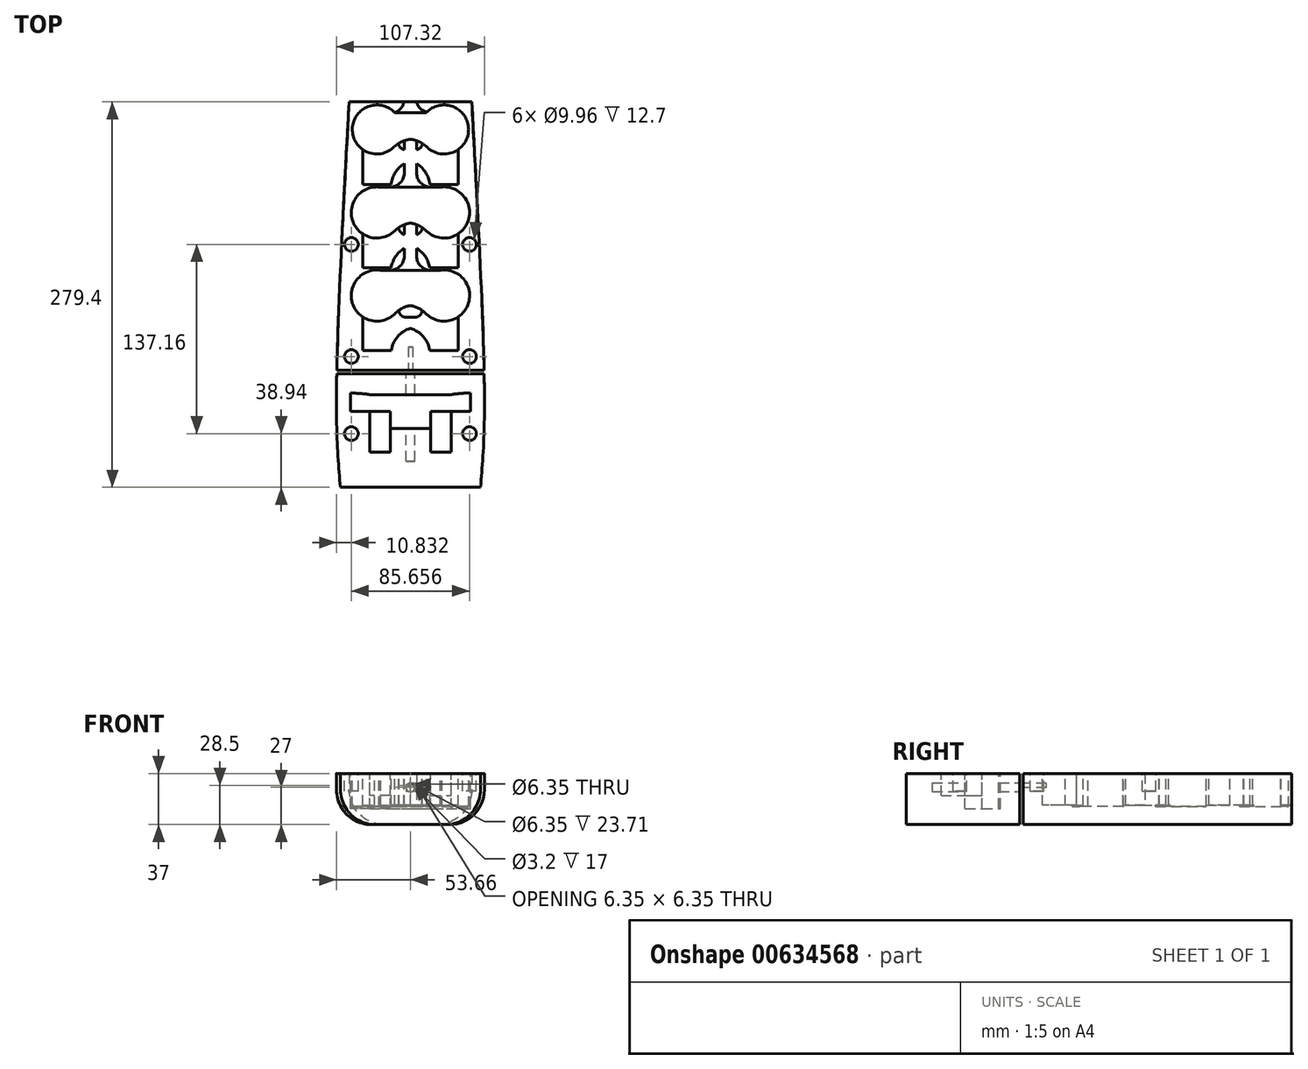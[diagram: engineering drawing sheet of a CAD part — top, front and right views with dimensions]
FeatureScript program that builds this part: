
annotation { "Feature Type Name" : "Feature", "Feature Type Description" : "" }
export const myFeature = defineFeature(function(context is Context, id is Id, definition is map)
    precondition{}
    {
        {
            var Q0;
            Q0=qCreatedBy(makeId("Top.planeOp"),FACE);
            var sketch = newSketch(context, id + "F0", { "sketchPlane" : qUnion([Q0])});
            skLineSegment(sketch, "E0", {"start": v(-44.45, 139.7) * mm, "end": v(44.45, 139.7) * mm});
            skLineSegment(sketch, "E1", {"start": v(0, 139.7) * mm, "end": v(0, -139.7) * mm, "construction": true});
            skLineSegment(sketch, "E2", {"start": v(0, -139.7) * mm, "end": v(-50.8, -139.7) * mm});
            skFitSpline(sketch, "E3", {"points": [v(-44.45, 139.7) * mm, v(-53.65, -82.07) * mm, v(-50.8, -139.7) * mm], "startDerivative": vector(-21.3, -389.22) * mm, "endDerivative": vector(12.22, -142.93) * mm});
            skFitSpline(sketch, "E4.MirrorCS", {"points": [v(44.45, 139.7) * mm, v(53.65, -82.07) * mm, v(50.8, -139.7) * mm], "startDerivative": vector(21.3, -389.22) * mm, "endDerivative": vector(-12.22, -142.93) * mm});
            skLineSegment(sketch, "E5.MirrorCS", {"start": v(0, -139.7) * mm, "end": v(50.8, -139.7) * mm});
            skSolve(sketch);
        }
        {
            var Q0;
            Q0=qSketchRegion(id+"F0",true);
            extrude(context, id + "F1", {"entities" : qUnion([Q0]), "depth" : 37 * mm, "offsetDistance" : 25.4 * mm});
        }
        {
            var Q0;
            Q0=makeQuery(id+"F1.opExtrude","CAP_EDGE",EDGE,{"disambiguationData":[OSD([sQuery(id+"F0.wireOp",EDGE,"E3")])],"isStart":true});
            var Q1;
            Q1=makeQuery(id+"F1.opExtrude","CAP_EDGE",EDGE,{"disambiguationData":[OSD([sQuery(id+"F0.wireOp",EDGE,"E4.MirrorCS")])],"isStart":true});
            fillet(context, id + "F2", {"entities" : qUnion([Q0, Q1]), "radius" : 25.4 * mm, "tangentPropagation" : true, "allowEdgeOverflow" : false});
        }
        {
            var Q0;
            Q0=makeQuery(id+"F1.opExtrude","CAP_FACE",FACE,{"disambiguationData":[OSD([sQuery(id+"F0.wireOp",EDGE,"E0"),sQuery(id+"F0.wireOp",EDGE,"E2"),sQuery(id+"F0.wireOp",EDGE,"E3"),sQuery(id+"F0.wireOp",EDGE,"E4.MirrorCS"),sQuery(id+"F0.wireOp",EDGE,"E5.MirrorCS")])],"isStart":false});
            var sketch = newSketch(context, id + "F3", { "sketchPlane" : qUnion([Q0])});
            skLineSegment(sketch, "E6.bottom", {"start": v(-34.7, 119.7) * mm, "end": v(-14, 119.7) * mm});
            skLineSegment(sketch, "E6.top", {"start": v(-34.7, 79.7) * mm, "end": v(-14, 79.7) * mm});
            skLineSegment(sketch, "E6.left", {"start": v(-34.7, 119.7) * mm, "end": v(-34.7, 79.7) * mm});
            skLineSegment(sketch, "E6.right", {"start": v(-14, 119.7) * mm, "end": v(-14, 79.7) * mm});
            skLineSegment(sketch, "E7", {"start": v(0, 139.7) * mm, "end": v(0, 0) * mm, "construction": true});
            skLineSegment(sketch, "E8", {"start": v(-38, 69.6) * mm, "end": v(36.85, 69.6) * mm, "construction": true});
            skLineSegment(sketch, "E9.MirrorCS", {"start": v(34.7, 119.7) * mm, "end": v(34.7, 79.7) * mm});
            skLineSegment(sketch, "E10.MirrorCS", {"start": v(14, 119.7) * mm, "end": v(14, 79.7) * mm});
            skLineSegment(sketch, "E11.MirrorCS", {"start": v(34.7, 79.7) * mm, "end": v(14, 79.7) * mm});
            skLineSegment(sketch, "E12.MirrorCS", {"start": v(34.7, 119.7) * mm, "end": v(14, 119.7) * mm});
            skLineSegment(sketch, "E13.MirrorCS", {"start": v(34.7, 19.5) * mm, "end": v(34.7, 59.5) * mm});
            skLineSegment(sketch, "E14.MirrorCS", {"start": v(-14, 19.5) * mm, "end": v(-14, 59.5) * mm});
            skLineSegment(sketch, "E15.MirrorCS", {"start": v(-34.7, 19.5) * mm, "end": v(-34.7, 59.5) * mm});
            skLineSegment(sketch, "E16.MirrorCS", {"start": v(-34.7, 59.5) * mm, "end": v(-14, 59.5) * mm});
            skLineSegment(sketch, "E17.MirrorCS", {"start": v(14, 19.5) * mm, "end": v(14, 59.5) * mm});
            skLineSegment(sketch, "E18.MirrorCS", {"start": v(34.7, 59.5) * mm, "end": v(14, 59.5) * mm});
            skLineSegment(sketch, "E19", {"start": v(-34.7, 19.5) * mm, "end": v(-14, 19.5) * mm});
            skLineSegment(sketch, "E20", {"start": v(14, 19.5) * mm, "end": v(34.7, 19.5) * mm});
            skLineSegment(sketch, "E21", {"start": v(-32.28, 9.4) * mm, "end": v(34.83, 9.4) * mm, "construction": true});
            skLineSegment(sketch, "E22.MirrorCS", {"start": v(-34.7, -40.7) * mm, "end": v(-14, -40.7) * mm});
            skLineSegment(sketch, "E23.MirrorCS", {"start": v(-34.7, -0.7) * mm, "end": v(-14, -0.7) * mm});
            skLineSegment(sketch, "E24.MirrorCS", {"start": v(34.7, -40.7) * mm, "end": v(14, -40.7) * mm});
            skLineSegment(sketch, "E25.MirrorCS", {"start": v(14, -0.7) * mm, "end": v(34.7, -0.7) * mm});
            skLineSegment(sketch, "E26.MirrorCS", {"start": v(-34.7, -0.7) * mm, "end": v(-34.7, -40.7) * mm});
            skLineSegment(sketch, "E27.MirrorCS", {"start": v(-14, -0.7) * mm, "end": v(-14, -40.7) * mm});
            skLineSegment(sketch, "E28.MirrorCS", {"start": v(34.7, -0.7) * mm, "end": v(34.7, -40.7) * mm});
            skLineSegment(sketch, "E29.MirrorCS", {"start": v(14, -0.7) * mm, "end": v(14, -40.7) * mm});
            skSolve(sketch);
        }
        {
            var Q0;
            Q0=qSketchRegion(id+"F3",true);
            extrude(context, id + "F4", {"entities" : qUnion([Q0]), "operationType" : NewBodyOperationType.REMOVE, "oppositeDirection" : true, "depth" : 23 * mm, "offsetDistance" : 25.4 * mm});
        }
        {
            var Q0;
            Q0=makeQuery(id+"F1.opExtrude","CAP_FACE",FACE,{"disambiguationData":[OSD([sQuery(id+"F0.wireOp",EDGE,"E0"),sQuery(id+"F0.wireOp",EDGE,"E2"),sQuery(id+"F0.wireOp",EDGE,"E3"),sQuery(id+"F0.wireOp",EDGE,"E4.MirrorCS"),sQuery(id+"F0.wireOp",EDGE,"E5.MirrorCS")])],"isStart":false});
            var sketch = newSketch(context, id + "F5", { "sketchPlane" : qUnion([Q0])});
            skCircle(sketch, "E30", {"center": v(-24.35, 119.7) * mm, "radius": 17.78 * mm});
            skCircle(sketch, "E31", {"center": v(24.35, 119.7) * mm, "radius": 17.78 * mm});
            skCircle(sketch, "E32", {"center": v(-24.35, 59.5) * mm, "radius": 18.54 * mm});
            skCircle(sketch, "E33", {"center": v(24.35, 59.5) * mm, "radius": 18.54 * mm});
            skCircle(sketch, "E34", {"center": v(-24.35, -0.7) * mm, "radius": 18.54 * mm});
            skCircle(sketch, "E35", {"center": v(24.35, -0.7) * mm, "radius": 18.54 * mm});
            skSolve(sketch);
        }
        {
            var Q0;
            Q0=qSketchRegion(id+"F5",true);
            extrude(context, id + "F6", {"entities" : qUnion([Q0]), "operationType" : NewBodyOperationType.REMOVE, "oppositeDirection" : true, "depth" : 24 * mm, "offsetDistance" : 25.4 * mm});
        }
        {
            var Q0;
            Q0=makeQuery(id+"F1.opExtrude","CAP_FACE",FACE,{"disambiguationData":[OSD([sQuery(id+"F0.wireOp",EDGE,"E0"),sQuery(id+"F0.wireOp",EDGE,"E2"),sQuery(id+"F0.wireOp",EDGE,"E3"),sQuery(id+"F0.wireOp",EDGE,"E4.MirrorCS"),sQuery(id+"F0.wireOp",EDGE,"E5.MirrorCS")])],"isStart":false});
            var sketch = newSketch(context, id + "F7", { "sketchPlane" : qUnion([Q0])});
            skSolve(sketch);
        }
        {
            var Q0;
            Q0=makeQuery(id+"F7.imprint","IMPRINT",FACE,{"disambiguationData":[TD([[makeQuery(id+"F7.imprint","IMPRINT",EDGE,{"derivedFrom":makeQuery(id+"F1.opExtrude","CAP_EDGE",EDGE,{"disambiguationData":[OSD([sQuery(id+"F0.wireOp",EDGE,"E0")])],"isStart":false})}),-1.0]])]});
            var sketch = newSketch(context, id + "F8", { "sketchPlane" : qUnion([Q0])});
            skLineSegment(sketch, "E36.bottom", {"start": v(-22.32, -16.47) * mm, "end": v(25.6, -16.47) * mm});
            skLineSegment(sketch, "E36.top", {"start": v(-22.32, -23.47) * mm, "end": v(25.6, -23.47) * mm});
            skLineSegment(sketch, "E36.left", {"start": v(-22.32, -16.47) * mm, "end": v(-22.32, -23.47) * mm});
            skLineSegment(sketch, "E36.right", {"start": v(25.6, -16.47) * mm, "end": v(25.6, -23.47) * mm});
            skLineSegment(sketch, "E37.bottom", {"start": v(-25.01, 43.48) * mm, "end": v(25.6, 43.48) * mm});
            skLineSegment(sketch, "E37.top", {"start": v(-25.01, 36.48) * mm, "end": v(25.6, 36.48) * mm});
            skLineSegment(sketch, "E37.left", {"start": v(-25.01, 43.48) * mm, "end": v(-25.01, 36.48) * mm});
            skLineSegment(sketch, "E37.right", {"start": v(25.6, 43.48) * mm, "end": v(25.6, 36.48) * mm});
            skLineSegment(sketch, "E38.bottom", {"start": v(-26.09, 104.99) * mm, "end": v(25.6, 104.99) * mm});
            skLineSegment(sketch, "E38.top", {"start": v(-26.09, 97.99) * mm, "end": v(25.6, 97.99) * mm});
            skLineSegment(sketch, "E38.left", {"start": v(-26.09, 104.99) * mm, "end": v(-26.09, 97.99) * mm});
            skLineSegment(sketch, "E38.right", {"start": v(25.6, 104.99) * mm, "end": v(25.6, 97.99) * mm});
            skSolve(sketch);
        }
        {
            var Q0;
            Q0=qSketchRegion(id+"F8",true);
            extrude(context, id + "F9", {"entities" : qUnion([Q0]), "operationType" : NewBodyOperationType.REMOVE, "oppositeDirection" : true, "depth" : 23 * mm, "offsetDistance" : 25.4 * mm});
        }
        {
            var Q0;
            Q0=makeQuery(id+"F9.boolean.opBoolean","INTERSECT",EDGE,{"derivedFrom":[makeQuery(id+"F4.boolean.opBoolean","COPY",FACE,{"derivedFrom":makeQuery(id+"F4.opExtrude","SWEPT_FACE",FACE,{"disambiguationData":[OSD([sQuery(id+"F3.wireOp",EDGE,"E6.right")])]})}),makeQuery(id+"F9.opExtrude","SWEPT_FACE",FACE,{"disambiguationData":[OSD([sQuery(id+"F8.wireOp",EDGE,"E38.bottom")])]})]});
            var Q1;
            Q1=makeQuery(id+"F9.boolean.opBoolean","INTERSECT",EDGE,{"derivedFrom":[makeQuery(id+"F4.boolean.opBoolean","COPY",FACE,{"derivedFrom":makeQuery(id+"F4.opExtrude","SWEPT_FACE",FACE,{"disambiguationData":[OSD([sQuery(id+"F3.wireOp",EDGE,"E10.MirrorCS")])]})}),makeQuery(id+"F9.opExtrude","SWEPT_FACE",FACE,{"disambiguationData":[OSD([sQuery(id+"F8.wireOp",EDGE,"E38.bottom")])]})]});
            var Q2;
            Q2=makeQuery(id+"F9.boolean.opBoolean","INTERSECT",EDGE,{"derivedFrom":[makeQuery(id+"F4.boolean.opBoolean","COPY",FACE,{"derivedFrom":makeQuery(id+"F4.opExtrude","SWEPT_FACE",FACE,{"disambiguationData":[OSD([sQuery(id+"F3.wireOp",EDGE,"E17.MirrorCS")])]})}),makeQuery(id+"F9.opExtrude","SWEPT_FACE",FACE,{"disambiguationData":[OSD([sQuery(id+"F8.wireOp",EDGE,"E37.bottom")])]})]});
            var Q3;
            Q3=makeQuery(id+"F9.boolean.opBoolean","INTERSECT",EDGE,{"derivedFrom":[makeQuery(id+"F4.boolean.opBoolean","COPY",FACE,{"derivedFrom":makeQuery(id+"F4.opExtrude","SWEPT_FACE",FACE,{"disambiguationData":[OSD([sQuery(id+"F3.wireOp",EDGE,"E14.MirrorCS")])]})}),makeQuery(id+"F9.opExtrude","SWEPT_FACE",FACE,{"disambiguationData":[OSD([sQuery(id+"F8.wireOp",EDGE,"E37.bottom")])]})]});
            var Q4;
            Q4=makeQuery(id+"F9.boolean.opBoolean","INTERSECT",EDGE,{"derivedFrom":[makeQuery(id+"F4.boolean.opBoolean","COPY",FACE,{"derivedFrom":makeQuery(id+"F4.opExtrude","SWEPT_FACE",FACE,{"disambiguationData":[OSD([sQuery(id+"F3.wireOp",EDGE,"E27.MirrorCS")])]})}),makeQuery(id+"F9.opExtrude","SWEPT_FACE",FACE,{"disambiguationData":[OSD([sQuery(id+"F8.wireOp",EDGE,"E36.bottom")])]})]});
            var Q5;
            Q5=makeQuery(id+"F9.boolean.opBoolean","INTERSECT",EDGE,{"derivedFrom":[makeQuery(id+"F4.boolean.opBoolean","COPY",FACE,{"derivedFrom":makeQuery(id+"F4.opExtrude","SWEPT_FACE",FACE,{"disambiguationData":[OSD([sQuery(id+"F3.wireOp",EDGE,"E29.MirrorCS")])]})}),makeQuery(id+"F9.opExtrude","SWEPT_FACE",FACE,{"disambiguationData":[OSD([sQuery(id+"F8.wireOp",EDGE,"E36.bottom")])]})]});
            fillet(context, id + "F10", {"entities" : qUnion([Q0, Q1, Q2, Q3, Q4, Q5]), "radius" : 12.7 * mm, "tangentPropagation" : true, "allowEdgeOverflow" : false});
        }
        {
            var Q0;
            Q0=makeQuery(id+"F7.imprint","IMPRINT",FACE,{"disambiguationData":[TD([[makeQuery(id+"F7.imprint","IMPRINT",EDGE,{"derivedFrom":makeQuery(id+"F1.opExtrude","CAP_EDGE",EDGE,{"disambiguationData":[OSD([sQuery(id+"F0.wireOp",EDGE,"E0")])],"isStart":false})}),-1.0]])]});
            var sketch = newSketch(context, id + "F11", { "sketchPlane" : qUnion([Q0])});
            skLineSegment(sketch, "E39.bottom", {"start": v(-65.32, -54.88) * mm, "end": v(72.26, -54.88) * mm});
            skLineSegment(sketch, "E39.top", {"start": v(-65.32, -57.24) * mm, "end": v(72.26, -57.24) * mm});
            skLineSegment(sketch, "E39.left", {"start": v(-65.32, -54.88) * mm, "end": v(-65.32, -57.24) * mm});
            skLineSegment(sketch, "E39.right", {"start": v(72.26, -54.88) * mm, "end": v(72.26, -57.24) * mm});
            skSolve(sketch);
        }
        {
            var Q0;
            Q0=qSketchRegion(id+"F11",true);
            extrude(context, id + "F12", {"entities" : qUnion([Q0]), "operationType" : NewBodyOperationType.REMOVE, "oppositeDirection" : true, "depth" : 508 * mm, "offsetDistance" : 25.4 * mm});
        }
        {
            var Q0;
            Q0=makeQuery(id+"F10.opFillet","BLEND_EDGE",EDGE,{"blendedFrom":[makeQuery(id+"F9.boolean.opBoolean","INTERSECT",EDGE,{"derivedFrom":[makeQuery(id+"F4.boolean.opBoolean","COPY",FACE,{"derivedFrom":makeQuery(id+"F4.opExtrude","SWEPT_FACE",FACE,{"disambiguationData":[OSD([sQuery(id+"F3.wireOp",EDGE,"E6.right")])]})}),makeQuery(id+"F9.opExtrude","SWEPT_FACE",FACE,{"disambiguationData":[OSD([sQuery(id+"F8.wireOp",EDGE,"E38.bottom")])]})]}),makeQuery(id+"F6.boolean.opBoolean","COPY",FACE,{"derivedFrom":makeQuery(id+"F6.opExtrude","SWEPT_FACE",FACE,{"disambiguationData":[OSD([sQuery(id+"F5.wireOp",EDGE,"E30")])]})})],"blendedInto":[makeQuery(id+"F6.boolean.opBoolean","COPY",FACE,{"derivedFrom":makeQuery(id+"F6.opExtrude","SWEPT_FACE",FACE,{"disambiguationData":[OSD([sQuery(id+"F5.wireOp",EDGE,"E30")])]})})]});
            var Q1;
            Q1=makeQuery(id+"F10.opFillet","BLEND_EDGE",EDGE,{"blendedFrom":[makeQuery(id+"F9.boolean.opBoolean","INTERSECT",EDGE,{"derivedFrom":[makeQuery(id+"F4.boolean.opBoolean","COPY",FACE,{"derivedFrom":makeQuery(id+"F4.opExtrude","SWEPT_FACE",FACE,{"disambiguationData":[OSD([sQuery(id+"F3.wireOp",EDGE,"E10.MirrorCS")])]})}),makeQuery(id+"F9.opExtrude","SWEPT_FACE",FACE,{"disambiguationData":[OSD([sQuery(id+"F8.wireOp",EDGE,"E38.bottom")])]})]}),makeQuery(id+"F6.boolean.opBoolean","COPY",FACE,{"derivedFrom":makeQuery(id+"F6.opExtrude","SWEPT_FACE",FACE,{"disambiguationData":[OSD([sQuery(id+"F5.wireOp",EDGE,"E31")])]})})],"blendedInto":[makeQuery(id+"F6.boolean.opBoolean","COPY",FACE,{"derivedFrom":makeQuery(id+"F6.opExtrude","SWEPT_FACE",FACE,{"disambiguationData":[OSD([sQuery(id+"F5.wireOp",EDGE,"E31")])]})})]});
            var Q2;
            Q2=makeQuery(id+"F10.opFillet","BLEND_EDGE",EDGE,{"blendedFrom":[makeQuery(id+"F9.boolean.opBoolean","INTERSECT",EDGE,{"derivedFrom":[makeQuery(id+"F4.boolean.opBoolean","COPY",FACE,{"derivedFrom":makeQuery(id+"F4.opExtrude","SWEPT_FACE",FACE,{"disambiguationData":[OSD([sQuery(id+"F3.wireOp",EDGE,"E14.MirrorCS")])]})}),makeQuery(id+"F9.opExtrude","SWEPT_FACE",FACE,{"disambiguationData":[OSD([sQuery(id+"F8.wireOp",EDGE,"E37.bottom")])]})]}),makeQuery(id+"F6.boolean.opBoolean","COPY",FACE,{"derivedFrom":makeQuery(id+"F6.opExtrude","SWEPT_FACE",FACE,{"disambiguationData":[OSD([sQuery(id+"F5.wireOp",EDGE,"E32")])]})})],"blendedInto":[makeQuery(id+"F6.boolean.opBoolean","COPY",FACE,{"derivedFrom":makeQuery(id+"F6.opExtrude","SWEPT_FACE",FACE,{"disambiguationData":[OSD([sQuery(id+"F5.wireOp",EDGE,"E32")])]})})]});
            var Q3;
            Q3=makeQuery(id+"F10.opFillet","BLEND_EDGE",EDGE,{"blendedFrom":[makeQuery(id+"F9.boolean.opBoolean","INTERSECT",EDGE,{"derivedFrom":[makeQuery(id+"F4.boolean.opBoolean","COPY",FACE,{"derivedFrom":makeQuery(id+"F4.opExtrude","SWEPT_FACE",FACE,{"disambiguationData":[OSD([sQuery(id+"F3.wireOp",EDGE,"E17.MirrorCS")])]})}),makeQuery(id+"F9.opExtrude","SWEPT_FACE",FACE,{"disambiguationData":[OSD([sQuery(id+"F8.wireOp",EDGE,"E37.bottom")])]})]}),makeQuery(id+"F6.boolean.opBoolean","COPY",FACE,{"derivedFrom":makeQuery(id+"F6.opExtrude","SWEPT_FACE",FACE,{"disambiguationData":[OSD([sQuery(id+"F5.wireOp",EDGE,"E33")])]})})],"blendedInto":[makeQuery(id+"F6.boolean.opBoolean","COPY",FACE,{"derivedFrom":makeQuery(id+"F6.opExtrude","SWEPT_FACE",FACE,{"disambiguationData":[OSD([sQuery(id+"F5.wireOp",EDGE,"E33")])]})})]});
            var Q4;
            Q4=makeQuery(id+"F10.opFillet","BLEND_EDGE",EDGE,{"blendedFrom":[makeQuery(id+"F9.boolean.opBoolean","INTERSECT",EDGE,{"derivedFrom":[makeQuery(id+"F4.boolean.opBoolean","COPY",FACE,{"derivedFrom":makeQuery(id+"F4.opExtrude","SWEPT_FACE",FACE,{"disambiguationData":[OSD([sQuery(id+"F3.wireOp",EDGE,"E27.MirrorCS")])]})}),makeQuery(id+"F9.opExtrude","SWEPT_FACE",FACE,{"disambiguationData":[OSD([sQuery(id+"F8.wireOp",EDGE,"E36.bottom")])]})]}),makeQuery(id+"F6.boolean.opBoolean","COPY",FACE,{"derivedFrom":makeQuery(id+"F6.opExtrude","SWEPT_FACE",FACE,{"disambiguationData":[OSD([sQuery(id+"F5.wireOp",EDGE,"E34")])]})})],"blendedInto":[makeQuery(id+"F6.boolean.opBoolean","COPY",FACE,{"derivedFrom":makeQuery(id+"F6.opExtrude","SWEPT_FACE",FACE,{"disambiguationData":[OSD([sQuery(id+"F5.wireOp",EDGE,"E34")])]})})]});
            var Q5;
            Q5=makeQuery(id+"F10.opFillet","BLEND_EDGE",EDGE,{"blendedFrom":[makeQuery(id+"F9.boolean.opBoolean","INTERSECT",EDGE,{"derivedFrom":[makeQuery(id+"F4.boolean.opBoolean","COPY",FACE,{"derivedFrom":makeQuery(id+"F4.opExtrude","SWEPT_FACE",FACE,{"disambiguationData":[OSD([sQuery(id+"F3.wireOp",EDGE,"E29.MirrorCS")])]})}),makeQuery(id+"F9.opExtrude","SWEPT_FACE",FACE,{"disambiguationData":[OSD([sQuery(id+"F8.wireOp",EDGE,"E36.bottom")])]})]}),makeQuery(id+"F6.boolean.opBoolean","COPY",FACE,{"derivedFrom":makeQuery(id+"F6.opExtrude","SWEPT_FACE",FACE,{"disambiguationData":[OSD([sQuery(id+"F5.wireOp",EDGE,"E35")])]})})],"blendedInto":[makeQuery(id+"F6.boolean.opBoolean","COPY",FACE,{"derivedFrom":makeQuery(id+"F6.opExtrude","SWEPT_FACE",FACE,{"disambiguationData":[OSD([sQuery(id+"F5.wireOp",EDGE,"E35")])]})})]});
            fillet(context, id + "F13", {"entities" : qUnion([Q0, Q1, Q2, Q3, Q4, Q5]), "radius" : 5.08 * mm, "tangentPropagation" : true, "allowEdgeOverflow" : false});
        }
        {
            var Q0;
            Q0=makeQuery(id+"F7.imprint","IMPRINT",FACE,{"disambiguationData":[TD([[makeQuery(id+"F7.imprint","IMPRINT",EDGE,{"derivedFrom":makeQuery(id+"F1.opExtrude","CAP_EDGE",EDGE,{"disambiguationData":[OSD([sQuery(id+"F0.wireOp",EDGE,"E0")])],"isStart":false})}),-1.0]])]});
            var sketch = newSketch(context, id + "F14", { "sketchPlane" : qUnion([Q0])});
            skLineSegment(sketch, "E40.bottom", {"start": v(-25.2, 131.93) * mm, "end": v(24.36, 131.93) * mm});
            skLineSegment(sketch, "E40.top", {"start": v(-25.2, 112.71) * mm, "end": v(24.36, 112.71) * mm});
            skLineSegment(sketch, "E40.left", {"start": v(-25.2, 131.93) * mm, "end": v(-25.2, 112.71) * mm});
            skLineSegment(sketch, "E40.right", {"start": v(24.36, 131.93) * mm, "end": v(24.36, 112.71) * mm});
            skLineSegment(sketch, "E41.bottom", {"start": v(-25.88, 77.98) * mm, "end": v(24.36, 77.98) * mm});
            skLineSegment(sketch, "E41.top", {"start": v(-25.88, 52.01) * mm, "end": v(24.36, 52.01) * mm});
            skLineSegment(sketch, "E41.left", {"start": v(-25.88, 77.98) * mm, "end": v(-25.88, 52.01) * mm});
            skLineSegment(sketch, "E41.right", {"start": v(24.36, 77.98) * mm, "end": v(24.36, 52.01) * mm});
            skLineSegment(sketch, "E42.bottom", {"start": v(-25.54, 17.62) * mm, "end": v(24.36, 17.62) * mm});
            skLineSegment(sketch, "E42.top", {"start": v(-25.54, -7.67) * mm, "end": v(24.36, -7.67) * mm});
            skLineSegment(sketch, "E42.left", {"start": v(-25.54, 17.62) * mm, "end": v(-25.54, -7.67) * mm});
            skLineSegment(sketch, "E42.right", {"start": v(24.36, 17.62) * mm, "end": v(24.36, -7.67) * mm});
            skSolve(sketch);
        }
        {
            var Q0;
            Q0=qSketchRegion(id+"F14",true);
            extrude(context, id + "F15", {"entities" : qUnion([Q0]), "operationType" : NewBodyOperationType.REMOVE, "oppositeDirection" : true, "depth" : 24 * mm, "offsetDistance" : 25.4 * mm});
        }
        {
            var Q0;
            Q0=makeQuery(id+"F9.boolean.opBoolean","INTERSECT",EDGE,{"derivedFrom":[makeQuery(id+"F4.boolean.opBoolean","COPY",FACE,{"derivedFrom":makeQuery(id+"F4.opExtrude","SWEPT_FACE",FACE,{"disambiguationData":[OSD([sQuery(id+"F3.wireOp",EDGE,"E6.right")])]})}),makeQuery(id+"F9.opExtrude","SWEPT_FACE",FACE,{"disambiguationData":[OSD([sQuery(id+"F8.wireOp",EDGE,"E38.top")])]})]});
            var Q1;
            Q1=makeQuery(id+"F9.boolean.opBoolean","INTERSECT",EDGE,{"derivedFrom":[makeQuery(id+"F4.boolean.opBoolean","COPY",FACE,{"derivedFrom":makeQuery(id+"F4.opExtrude","SWEPT_FACE",FACE,{"disambiguationData":[OSD([sQuery(id+"F3.wireOp",EDGE,"E10.MirrorCS")])]})}),makeQuery(id+"F9.opExtrude","SWEPT_FACE",FACE,{"disambiguationData":[OSD([sQuery(id+"F8.wireOp",EDGE,"E38.top")])]})]});
            var Q2;
            Q2=makeQuery(id+"F15.boolean.opBoolean","INTERSECT",EDGE,{"derivedFrom":[makeQuery(id+"F6.boolean.opBoolean","COPY",FACE,{"derivedFrom":makeQuery(id+"F6.opExtrude","SWEPT_FACE",FACE,{"disambiguationData":[OSD([sQuery(id+"F5.wireOp",EDGE,"E31")])]})}),makeQuery(id+"F15.opExtrude","SWEPT_FACE",FACE,{"disambiguationData":[OSD([sQuery(id+"F14.wireOp",EDGE,"E40.top")])]})]});
            var Q3;
            Q3=makeQuery(id+"F15.boolean.opBoolean","INTERSECT",EDGE,{"derivedFrom":[makeQuery(id+"F6.boolean.opBoolean","COPY",FACE,{"derivedFrom":makeQuery(id+"F6.opExtrude","SWEPT_FACE",FACE,{"disambiguationData":[OSD([sQuery(id+"F5.wireOp",EDGE,"E30")])]})}),makeQuery(id+"F15.opExtrude","SWEPT_FACE",FACE,{"disambiguationData":[OSD([sQuery(id+"F14.wireOp",EDGE,"E40.top")])]})]});
            var Q4;
            Q4=makeQuery(id+"F15.boolean.opBoolean","INTERSECT",EDGE,{"derivedFrom":[makeQuery(id+"F6.boolean.opBoolean","COPY",FACE,{"derivedFrom":makeQuery(id+"F6.opExtrude","SWEPT_FACE",FACE,{"disambiguationData":[OSD([sQuery(id+"F5.wireOp",EDGE,"E32")])]})}),makeQuery(id+"F15.opExtrude","SWEPT_FACE",FACE,{"disambiguationData":[OSD([sQuery(id+"F14.wireOp",EDGE,"E41.top")])]})]});
            var Q5;
            Q5=makeQuery(id+"F15.boolean.opBoolean","INTERSECT",EDGE,{"derivedFrom":[makeQuery(id+"F6.boolean.opBoolean","COPY",FACE,{"derivedFrom":makeQuery(id+"F6.opExtrude","SWEPT_FACE",FACE,{"disambiguationData":[OSD([sQuery(id+"F5.wireOp",EDGE,"E33")])]})}),makeQuery(id+"F15.opExtrude","SWEPT_FACE",FACE,{"disambiguationData":[OSD([sQuery(id+"F14.wireOp",EDGE,"E41.top")])]})]});
            var Q6;
            Q6=makeQuery(id+"F9.boolean.opBoolean","INTERSECT",EDGE,{"derivedFrom":[makeQuery(id+"F4.boolean.opBoolean","COPY",FACE,{"derivedFrom":makeQuery(id+"F4.opExtrude","SWEPT_FACE",FACE,{"disambiguationData":[OSD([sQuery(id+"F3.wireOp",EDGE,"E14.MirrorCS")])]})}),makeQuery(id+"F9.opExtrude","SWEPT_FACE",FACE,{"disambiguationData":[OSD([sQuery(id+"F8.wireOp",EDGE,"E37.top")])]})]});
            var Q7;
            Q7=makeQuery(id+"F9.boolean.opBoolean","INTERSECT",EDGE,{"derivedFrom":[makeQuery(id+"F4.boolean.opBoolean","COPY",FACE,{"derivedFrom":makeQuery(id+"F4.opExtrude","SWEPT_FACE",FACE,{"disambiguationData":[OSD([sQuery(id+"F3.wireOp",EDGE,"E17.MirrorCS")])]})}),makeQuery(id+"F9.opExtrude","SWEPT_FACE",FACE,{"disambiguationData":[OSD([sQuery(id+"F8.wireOp",EDGE,"E37.top")])]})]});
            var Q8;
            Q8=makeQuery(id+"F15.boolean.opBoolean","INTERSECT",EDGE,{"derivedFrom":[makeQuery(id+"F6.boolean.opBoolean","COPY",FACE,{"derivedFrom":makeQuery(id+"F6.opExtrude","SWEPT_FACE",FACE,{"disambiguationData":[OSD([sQuery(id+"F5.wireOp",EDGE,"E34")])]})}),makeQuery(id+"F15.opExtrude","SWEPT_FACE",FACE,{"disambiguationData":[OSD([sQuery(id+"F14.wireOp",EDGE,"E42.top")])]})]});
            var Q9;
            Q9=makeQuery(id+"F15.boolean.opBoolean","INTERSECT",EDGE,{"derivedFrom":[makeQuery(id+"F6.boolean.opBoolean","COPY",FACE,{"derivedFrom":makeQuery(id+"F6.opExtrude","SWEPT_FACE",FACE,{"disambiguationData":[OSD([sQuery(id+"F5.wireOp",EDGE,"E35")])]})}),makeQuery(id+"F15.opExtrude","SWEPT_FACE",FACE,{"disambiguationData":[OSD([sQuery(id+"F14.wireOp",EDGE,"E42.top")])]})]});
            var Q10;
            Q10=makeQuery(id+"F9.boolean.opBoolean","INTERSECT",EDGE,{"derivedFrom":[makeQuery(id+"F4.boolean.opBoolean","COPY",FACE,{"derivedFrom":makeQuery(id+"F4.opExtrude","SWEPT_FACE",FACE,{"disambiguationData":[OSD([sQuery(id+"F3.wireOp",EDGE,"E27.MirrorCS")])]})}),makeQuery(id+"F9.opExtrude","SWEPT_FACE",FACE,{"disambiguationData":[OSD([sQuery(id+"F8.wireOp",EDGE,"E36.top")])]})]});
            var Q11;
            Q11=makeQuery(id+"F9.boolean.opBoolean","INTERSECT",EDGE,{"derivedFrom":[makeQuery(id+"F4.boolean.opBoolean","COPY",FACE,{"derivedFrom":makeQuery(id+"F4.opExtrude","SWEPT_FACE",FACE,{"disambiguationData":[OSD([sQuery(id+"F3.wireOp",EDGE,"E29.MirrorCS")])]})}),makeQuery(id+"F9.opExtrude","SWEPT_FACE",FACE,{"disambiguationData":[OSD([sQuery(id+"F8.wireOp",EDGE,"E36.top")])]})]});
            fillet(context, id + "F16", {"entities" : qUnion([Q0, Q1, Q2, Q3, Q4, Q5, Q6, Q7, Q8, Q9, Q10, Q11]), "radius" : 20.32 * mm, "tangentPropagation" : true, "allowEdgeOverflow" : false});
        }
        {
            var Q0;
            Q0=makeQuery(id+"F7.imprint","IMPRINT",FACE,{"disambiguationData":[TD([[makeQuery(id+"F7.imprint","IMPRINT",EDGE,{"derivedFrom":makeQuery(id+"F1.opExtrude","CAP_EDGE",EDGE,{"disambiguationData":[OSD([sQuery(id+"F0.wireOp",EDGE,"E0")])],"isStart":false})}),-1.0]])]});
            var sketch = newSketch(context, id + "F17", { "sketchPlane" : qUnion([Q0])});
            skLineSegment(sketch, "E43", {"start": v(0, 140.03) * mm, "end": v(0, 16.27) * mm, "construction": true});
            skLineSegment(sketch, "E44", {"start": v(4.47, 16.27) * mm, "end": v(4.47, 143.3) * mm});
            skLineSegment(sketch, "E45", {"start": v(4.47, 143.3) * mm, "end": v(0, 140.03) * mm});
            skLineSegment(sketch, "E46.MirrorCS", {"start": v(-4.47, 16.27) * mm, "end": v(-4.47, 143.3) * mm});
            skLineSegment(sketch, "E47", {"start": v(-4.47, 143.3) * mm, "end": v(0, 140.03) * mm});
            skLineSegment(sketch, "E48", {"start": v(-4.47, 16.27) * mm, "end": v(-4.47, 8.85) * mm});
            skLineSegment(sketch, "E49", {"start": v(-4.47, 8.85) * mm, "end": v(4.47, 16.27) * mm});
            skSolve(sketch);
        }
        {
            var Q0;
            Q0=qSketchRegion(id+"F17",true);
            var Q1;
            Q1=qConstructionFilter(qBodyType(qCreatedBy(id+"F17",EDGE),BodyType.WIRE),ConstructionObject.NO);
            extrude(context, id + "F18", {"entities" : qUnion([Q0]), "operationType" : NewBodyOperationType.REMOVE, "surfaceEntities" : qUnion([Q1]), "oppositeDirection" : true, "depth" : 23 * mm, "offsetDistance" : 25.4 * mm});
        }
        {
            var Q0;
            Q0=makeQuery(id+"F18.boolean.opBoolean","INTERSECT",EDGE,{"derivedFrom":[makeQuery(id+"F15.boolean.opBoolean","COPY",FACE,{"derivedFrom":makeQuery(id+"F15.opExtrude","SWEPT_FACE",FACE,{"disambiguationData":[OSD([sQuery(id+"F14.wireOp",EDGE,"E42.bottom")])]})}),makeQuery(id+"F18.opExtrude","SWEPT_FACE",FACE,{"disambiguationData":[OSD([sQuery(id+"F17.wireOp",EDGE,"E46.MirrorCS"),sQuery(id+"F17.wireOp",EDGE,"E48")])]})]});
            var Q1;
            Q1=makeQuery(id+"F18.boolean.opBoolean","INTERSECT",EDGE,{"derivedFrom":[makeQuery(id+"F15.boolean.opBoolean","COPY",FACE,{"derivedFrom":makeQuery(id+"F15.opExtrude","SWEPT_FACE",FACE,{"disambiguationData":[OSD([sQuery(id+"F14.wireOp",EDGE,"E42.bottom")])]})}),makeQuery(id+"F18.opExtrude","SWEPT_FACE",FACE,{"disambiguationData":[OSD([sQuery(id+"F17.wireOp",EDGE,"E44")])]})]});
            var Q2;
            {var subQ0=sQuery(id+"F5.wireOp",EDGE,"E33");var subQ2=sQuery(id+"F14.wireOp",EDGE,"E41.bottom");Q2=makeQuery(id+"F18.boolean.opBoolean","INTERSECT",EDGE,{"derivedFrom":[makeQuery(id+"F15.boolean.opBoolean","COPY",FACE,{"disambiguationData":[TD([makeQuery(id+"F6.boolean.opBoolean","COPY",FACE,{"derivedFrom":makeQuery(id+"F6.opExtrude","SWEPT_FACE",FACE,{"disambiguationData":[OSD([subQ0])]})})])],"derivedFrom":makeQuery(id+"F15.opExtrude","SWEPT_FACE",FACE,{"disambiguationData":[OSD([subQ2])]})}),makeQuery(id+"F18.opExtrude","SWEPT_FACE",FACE,{"disambiguationData":[OSD([sQuery(id+"F17.wireOp",EDGE,"E46.MirrorCS"),sQuery(id+"F17.wireOp",EDGE,"E48")])]})]});}
            var Q3;
            {var subQ0=sQuery(id+"F5.wireOp",EDGE,"E33");var subQ2=sQuery(id+"F14.wireOp",EDGE,"E41.bottom");Q3=makeQuery(id+"F18.boolean.opBoolean","INTERSECT",EDGE,{"derivedFrom":[makeQuery(id+"F15.boolean.opBoolean","COPY",FACE,{"disambiguationData":[TD([makeQuery(id+"F6.boolean.opBoolean","COPY",FACE,{"derivedFrom":makeQuery(id+"F6.opExtrude","SWEPT_FACE",FACE,{"disambiguationData":[OSD([subQ0])]})})])],"derivedFrom":makeQuery(id+"F15.opExtrude","SWEPT_FACE",FACE,{"disambiguationData":[OSD([subQ2])]})}),makeQuery(id+"F18.opExtrude","SWEPT_FACE",FACE,{"disambiguationData":[OSD([sQuery(id+"F17.wireOp",EDGE,"E44")])]})]});}
            var Q4;
            Q4=makeQuery(id+"F18.boolean.opBoolean","INTERSECT",EDGE,{"derivedFrom":[makeQuery(id+"F15.boolean.opBoolean","COPY",FACE,{"derivedFrom":makeQuery(id+"F15.opExtrude","SWEPT_FACE",FACE,{"disambiguationData":[OSD([sQuery(id+"F14.wireOp",EDGE,"E40.bottom")])]})}),makeQuery(id+"F18.opExtrude","SWEPT_FACE",FACE,{"disambiguationData":[OSD([sQuery(id+"F17.wireOp",EDGE,"E46.MirrorCS"),sQuery(id+"F17.wireOp",EDGE,"E48")])]})]});
            var Q5;
            Q5=makeQuery(id+"F18.boolean.opBoolean","INTERSECT",EDGE,{"derivedFrom":[makeQuery(id+"F15.boolean.opBoolean","COPY",FACE,{"derivedFrom":makeQuery(id+"F15.opExtrude","SWEPT_FACE",FACE,{"disambiguationData":[OSD([sQuery(id+"F14.wireOp",EDGE,"E40.bottom")])]})}),makeQuery(id+"F18.opExtrude","SWEPT_FACE",FACE,{"disambiguationData":[OSD([sQuery(id+"F17.wireOp",EDGE,"E44")])]})]});
            fillet(context, id + "F19", {"entities" : qUnion([Q0, Q1, Q2, Q3, Q4, Q5]), "radius" : 10.16 * mm, "tangentPropagation" : true, "allowEdgeOverflow" : false});
        }
        {
            var Q0;
            Q0=makeQuery(id+"F7.imprint","IMPRINT",FACE,{"disambiguationData":[TD([[makeQuery(id+"F7.imprint","IMPRINT",EDGE,{"derivedFrom":makeQuery(id+"F1.opExtrude","CAP_EDGE",EDGE,{"disambiguationData":[OSD([sQuery(id+"F0.wireOp",EDGE,"E0")])],"isStart":false})}),-1.0]])]});
            var sketch = newSketch(context, id + "F20", { "sketchPlane" : qUnion([Q0])});
            skCircle(sketch, "E50", {"center": v(-42.83, -44.88) * mm, "radius": 4.98 * mm});
            skLineSegment(sketch, "E51", {"start": v(-116.6, -4.24) * mm, "end": v(126.87, -4.24) * mm, "construction": true});
            skLineSegment(sketch, "E52", {"start": v(-120.64, -72.82) * mm, "end": v(118.78, -72.82) * mm, "construction": true});
            skLineSegment(sketch, "E53", {"start": v(0, 0) * mm, "end": v(0, -111.87) * mm, "construction": true});
            skCircle(sketch, "E54.MirrorC", {"center": v(-42.83, 36.4) * mm, "radius": 4.98 * mm});
            skCircle(sketch, "E55.MirrorC", {"center": v(-42.83, -100.76) * mm, "radius": 4.98 * mm});
            skCircle(sketch, "E56.MirrorC", {"center": v(42.83, -44.88) * mm, "radius": 4.98 * mm});
            skCircle(sketch, "E57.MirrorC", {"center": v(42.83, 36.4) * mm, "radius": 4.98 * mm});
            skCircle(sketch, "E58.MirrorC", {"center": v(42.83, -100.76) * mm, "radius": 4.98 * mm});
            skSolve(sketch);
        }
        {
            var Q0;
            Q0=qSketchRegion(id+"F20",true);
            extrude(context, id + "F21", {"entities" : qUnion([Q0]), "operationType" : NewBodyOperationType.REMOVE, "oppositeDirection" : true, "depth" : 12.7 * mm, "offsetDistance" : 25.4 * mm});
        }
        {
            var Q0;
            Q0=makeQuery(id+"F7.imprint","IMPRINT",FACE,{"disambiguationData":[TD([[makeQuery(id+"F7.imprint","IMPRINT",EDGE,{"derivedFrom":makeQuery(id+"F1.opExtrude","CAP_EDGE",EDGE,{"disambiguationData":[OSD([sQuery(id+"F0.wireOp",EDGE,"E0")])],"isStart":false})}),-1.0]])]});
            var sketch = newSketch(context, id + "F22", { "sketchPlane" : qUnion([Q0])});
            skLineSegment(sketch, "E59", {"start": v(-22.12, 0) * mm, "end": v(-22.12, -180.21) * mm, "construction": true});
            skLineSegment(sketch, "E60", {"start": v(-22.12, -114.23) * mm, "end": v(-14.62, -114.23) * mm});
            skLineSegment(sketch, "E61", {"start": v(-14.62, -114.23) * mm, "end": v(-14.62, -79.23) * mm});
            skLineSegment(sketch, "E62", {"start": v(-14.62, -79.23) * mm, "end": v(-22.12, -79.23) * mm});
            skLineSegment(sketch, "E63.MirrorCS", {"start": v(-29.62, -79.23) * mm, "end": v(-22.12, -79.23) * mm});
            skLineSegment(sketch, "E64.MirrorCS", {"start": v(-29.62, -114.23) * mm, "end": v(-29.62, -79.23) * mm});
            skLineSegment(sketch, "E65.MirrorCS", {"start": v(-22.12, -114.23) * mm, "end": v(-29.62, -114.23) * mm});
            skLineSegment(sketch, "E66", {"start": v(0, 0) * mm, "end": v(0, -136.82) * mm, "construction": true});
            skLineSegment(sketch, "E67.MirrorCS", {"start": v(29.62, -114.23) * mm, "end": v(29.62, -79.23) * mm});
            skLineSegment(sketch, "E68.MirrorCS", {"start": v(22.12, -114.23) * mm, "end": v(29.62, -114.23) * mm});
            skLineSegment(sketch, "E69.MirrorCS", {"start": v(22.12, -114.23) * mm, "end": v(14.62, -114.23) * mm});
            skLineSegment(sketch, "E70.MirrorCS", {"start": v(14.62, -114.23) * mm, "end": v(14.62, -79.23) * mm});
            skLineSegment(sketch, "E71.MirrorCS", {"start": v(29.62, -79.23) * mm, "end": v(22.12, -79.23) * mm});
            skLineSegment(sketch, "E72.MirrorCS", {"start": v(14.62, -79.23) * mm, "end": v(22.12, -79.23) * mm});
            skSolve(sketch);
        }
        {
            var Q0;
            Q0=qSketchRegion(id+"F22",true);
            extrude(context, id + "F23", {"entities" : qUnion([Q0]), "operationType" : NewBodyOperationType.REMOVE, "oppositeDirection" : true, "depth" : 16 * mm, "offsetDistance" : 25.4 * mm});
        }
        {
            var Q0;
            Q0=makeQuery(id+"F12.boolean.opBoolean","COPY",FACE,{"derivedFrom":makeQuery(id+"F12.opExtrude","SWEPT_FACE",FACE,{"disambiguationData":[OSD([sQuery(id+"F11.wireOp",EDGE,"E39.bottom")])]})});
            var sketch = newSketch(context, id + "F24", { "sketchPlane" : qUnion([Q0])});
            skLineSegment(sketch, "E73", {"start": v(0, 37) * mm, "end": v(0, 20.57) * mm, "construction": true});
            skPoint(sketch, "E73.endSnap0", {"position": v(0, 37) * mm});
            skCircle(sketch, "E74", {"center": v(0, 28.5) * mm, "radius": 1.6 * mm});
            skSolve(sketch);
        }
        {
            var Q0;
            Q0=qSketchRegion(id+"F24",true);
            extrude(context, id + "F25", {"entities" : qUnion([Q0]), "operationType" : NewBodyOperationType.REMOVE, "oppositeDirection" : true, "depth" : 17 * mm, "offsetDistance" : 25.4 * mm});
        }
        {
            var Q0;
            Q0=makeQuery(id+"F12.boolean.opBoolean","COPY",FACE,{"derivedFrom":makeQuery(id+"F12.opExtrude","SWEPT_FACE",FACE,{"disambiguationData":[OSD([sQuery(id+"F11.wireOp",EDGE,"E39.top")])]})});
            var sketch = newSketch(context, id + "F26", { "sketchPlane" : qUnion([Q0])});
            skLineSegment(sketch, "E75", {"start": v(0, 0) * mm, "end": v(0, 38.77) * mm, "construction": true});
            skPoint(sketch, "E75.endSnap0", {"position": v(0, 37) * mm});
            skCircle(sketch, "E76", {"center": v(0, 27) * mm, "radius": 3.18 * mm});
            skSolve(sketch);
        }
        {
            var Q0;
            Q0=qSketchRegion(id+"F26",true);
            extrude(context, id + "F27", {"entities" : qUnion([Q0]), "operationType" : NewBodyOperationType.REMOVE, "oppositeDirection" : true, "depth" : 63.5 * mm, "offsetDistance" : 25.4 * mm});
        }
        {
            var Q0;
            {var subQ0=sQuery(id+"F0.wireOp",EDGE,"E5.MirrorCS");var subQ1=sQuery(id+"F0.wireOp",EDGE,"E2");var subQ2=sQuery(id+"F0.wireOp",EDGE,"E3");var subQ3=sQuery(id+"F0.wireOp",EDGE,"E4.MirrorCS");Q0=makeQuery(id+"F12.boolean.opBoolean","SPLIT",FACE,{"disambiguationData":[TD([makeQuery(id+"F12.opExtrude","SWEPT_FACE",FACE,{"disambiguationData":[OSD([sQuery(id+"F11.wireOp",EDGE,"E39.top")])]})])],"derivedFrom":makeQuery(id+"F1.opExtrude","CAP_FACE",FACE,{"disambiguationData":[OSD([sQuery(id+"F0.wireOp",EDGE,"E0"),subQ1,subQ2,subQ3,subQ0])],"isStart":false})});}
            var sketch = newSketch(context, id + "F28", { "sketchPlane" : qUnion([Q0])});
            skLineSegment(sketch, "E77", {"start": v(0, -57.24) * mm, "end": v(0, -113.5) * mm, "construction": true});
            skLineSegment(sketch, "E78.bottom", {"start": v(-14.62, -79.23) * mm, "end": v(0, -79.23) * mm});
            skLineSegment(sketch, "E78.top", {"start": v(-14.62, -97.03) * mm, "end": v(0, -97.03) * mm});
            skLineSegment(sketch, "E78.left", {"start": v(-14.62, -79.23) * mm, "end": v(-14.62, -97.03) * mm});
            skLineSegment(sketch, "E78.right", {"start": v(0, -79.23) * mm, "end": v(0, -97.03) * mm});
            skLineSegment(sketch, "E79.bottom", {"start": v(-29.62, -79.23) * mm, "end": v(-14.62, -79.23) * mm});
            skLineSegment(sketch, "E79.top", {"start": v(-29.62, -84.55) * mm, "end": v(-14.62, -84.55) * mm});
            skLineSegment(sketch, "E79.left", {"start": v(-29.62, -79.23) * mm, "end": v(-29.62, -84.55) * mm});
            skLineSegment(sketch, "E79.right", {"start": v(-14.62, -79.23) * mm, "end": v(-14.62, -84.55) * mm});
            skLineSegment(sketch, "E80.bottom", {"start": v(-29.62, -79.23) * mm, "end": v(0, -79.23) * mm});
            skLineSegment(sketch, "E80.top", {"start": v(-29.62, -72.47) * mm, "end": v(0, -72.47) * mm});
            skLineSegment(sketch, "E80.left", {"start": v(-29.62, -79.23) * mm, "end": v(-29.62, -72.47) * mm});
            skLineSegment(sketch, "E80.right", {"start": v(0, -79.23) * mm, "end": v(0, -72.47) * mm});
            skLineSegment(sketch, "E81.bottom", {"start": v(0, -97.03) * mm, "end": v(0, -97.03) * mm});
            skLineSegment(sketch, "E81.top", {"start": v(0, -72.47) * mm, "end": v(0, -72.47) * mm});
            skLineSegment(sketch, "E81.left", {"start": v(0, -97.03) * mm, "end": v(0, -72.47) * mm});
            skLineSegment(sketch, "E81.right", {"start": v(0, -97.03) * mm, "end": v(0, -72.47) * mm});
            skLineSegment(sketch, "E82.bottom", {"start": v(-29.62, -84.55) * mm, "end": v(-43.57, -84.55) * mm});
            skLineSegment(sketch, "E82.top", {"start": v(-29.62, -71.42) * mm, "end": v(-43.57, -71.42) * mm});
            skLineSegment(sketch, "E82.left", {"start": v(-29.62, -84.55) * mm, "end": v(-29.62, -71.42) * mm});
            skLineSegment(sketch, "E82.right", {"start": v(-43.57, -84.55) * mm, "end": v(-43.57, -71.42) * mm});
            skLineSegment(sketch, "E83.MirrorCS", {"start": v(29.62, -84.55) * mm, "end": v(29.62, -71.42) * mm});
            skLineSegment(sketch, "E84.MirrorCS", {"start": v(29.62, -84.55) * mm, "end": v(43.57, -84.55) * mm});
            skLineSegment(sketch, "E85.MirrorCS", {"start": v(14.62, -79.23) * mm, "end": v(14.62, -97.03) * mm});
            skLineSegment(sketch, "E86.MirrorCS", {"start": v(29.62, -79.23) * mm, "end": v(14.62, -79.23) * mm});
            skLineSegment(sketch, "E87.MirrorCS", {"start": v(43.57, -84.55) * mm, "end": v(43.57, -71.42) * mm});
            skLineSegment(sketch, "E88.MirrorCS", {"start": v(29.62, -84.55) * mm, "end": v(14.62, -84.55) * mm});
            skLineSegment(sketch, "E89.MirrorCS", {"start": v(29.62, -79.23) * mm, "end": v(29.62, -84.55) * mm});
            skLineSegment(sketch, "E90.MirrorCS", {"start": v(14.62, -79.23) * mm, "end": v(14.62, -84.55) * mm});
            skLineSegment(sketch, "E91.MirrorCS", {"start": v(29.62, -71.42) * mm, "end": v(43.57, -71.42) * mm});
            skLineSegment(sketch, "E92.MirrorCS", {"start": v(29.62, -79.23) * mm, "end": v(29.62, -72.47) * mm});
            skLineSegment(sketch, "E93.MirrorCS", {"start": v(14.62, -97.03) * mm, "end": v(0, -97.03) * mm});
            skLineSegment(sketch, "E94.MirrorCS", {"start": v(29.62, -72.47) * mm, "end": v(0, -72.47) * mm});
            skSolve(sketch);
        }
        {
            var Q0;
            Q0=qSketchRegion(id+"F28",true);
            extrude(context, id + "F29", {"entities" : qUnion([Q0]), "operationType" : NewBodyOperationType.REMOVE, "oppositeDirection" : true, "depth" : 25.4 * mm, "offsetDistance" : 25.4 * mm});
        }
        {
            var Q0;
            Q0=makeQuery(id+"F29.boolean.opBoolean","COPY",EDGE,{"derivedFrom":makeQuery(id+"F29.opExtrude","SWEPT_EDGE",EDGE,{"disambiguationData":[OSD([sQuery(id+"F28.wireOp",EDGE,"E82.top"),sQuery(id+"F28.wireOp",EDGE,"E82.left")])]})});
            fillet(context, id + "F30", {"entities" : qUnion([Q0]), "radius" : 88.9 * mm, "tangentPropagation" : true, "allowEdgeOverflow" : false});
        }
        {
            var Q0;
            Q0=makeQuery(id+"F29.boolean.opBoolean","COPY",EDGE,{"derivedFrom":makeQuery(id+"F29.opExtrude","SWEPT_EDGE",EDGE,{"disambiguationData":[OSD([sQuery(id+"F28.wireOp",EDGE,"E83.MirrorCS"),sQuery(id+"F28.wireOp",EDGE,"E91.MirrorCS")])]})});
            fillet(context, id + "F31", {"entities" : qUnion([Q0]), "radius" : 73.66 * mm, "tangentPropagation" : true, "allowEdgeOverflow" : false});
        }
    });
